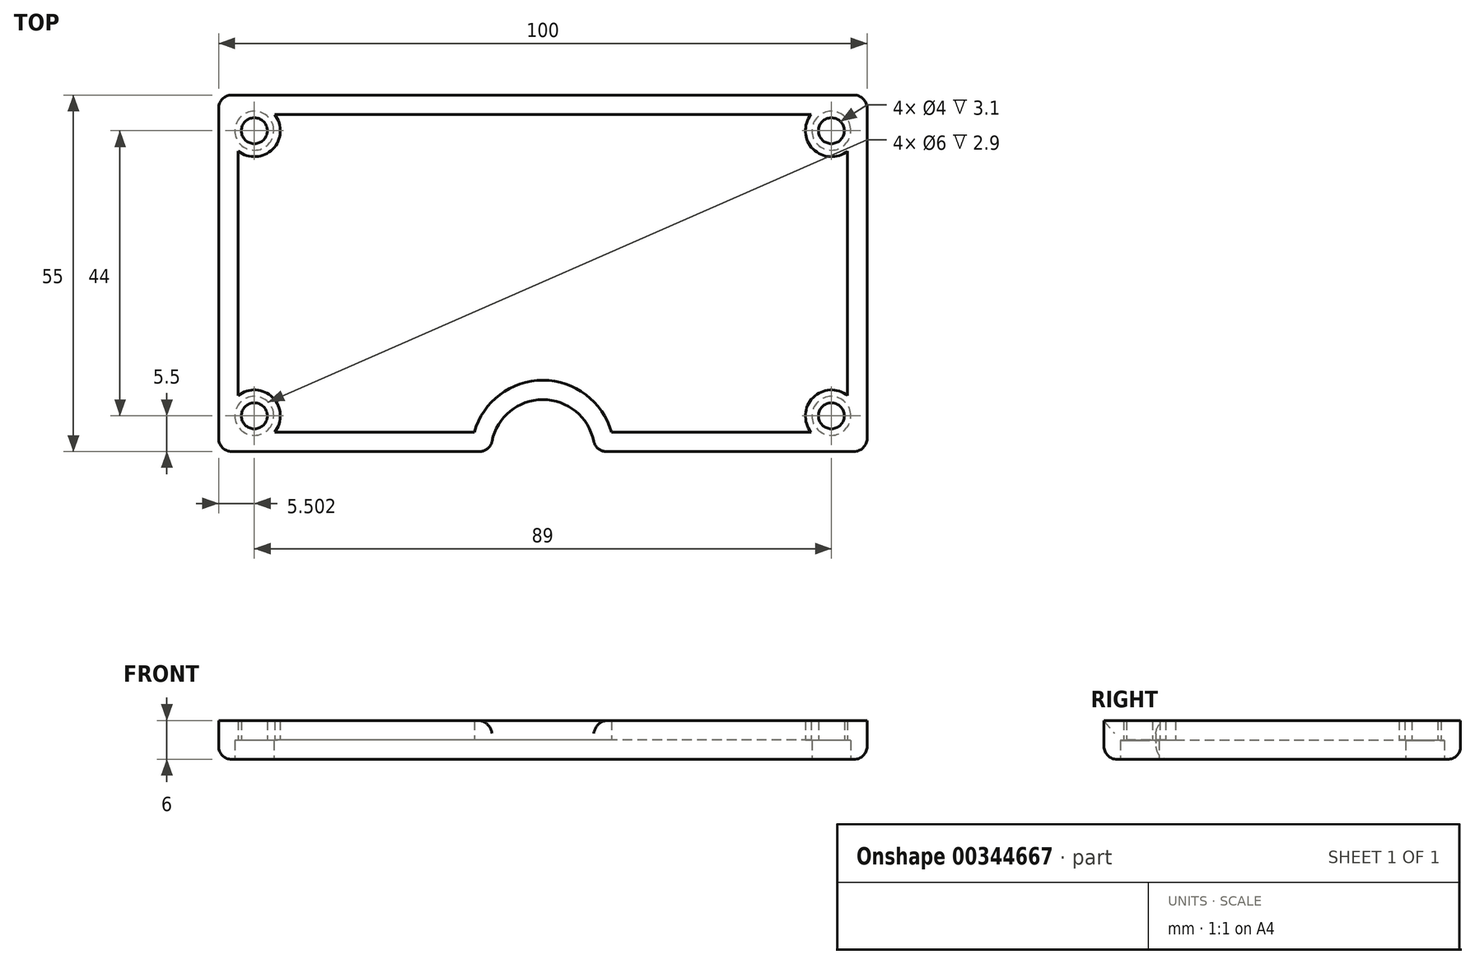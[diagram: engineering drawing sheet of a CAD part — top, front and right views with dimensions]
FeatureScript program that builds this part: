
annotation { "Feature Type Name" : "Feature", "Feature Type Description" : "" }
export const myFeature = defineFeature(function(context is Context, id is Id, definition is map)
    precondition{}
    {
        {
            var Q0;
            Q0=qCreatedBy(makeId("Top.planeOp"),FACE);
            var sketch = newSketch(context, id + "F0", { "sketchPlane" : qUnion([Q0])});
            skLineSegment(sketch, "E0.bottom", {"start": v(-50, 27.5) * mm, "end": v(50, 27.5) * mm});
            skLineSegment(sketch, "E0.top", {"start": v(-50, -27.5) * mm, "end": v(50, -27.5) * mm});
            skLineSegment(sketch, "E0.left", {"start": v(-50, 27.5) * mm, "end": v(-50, -27.5) * mm});
            skLineSegment(sketch, "E0.right", {"start": v(50, 27.5) * mm, "end": v(50, -27.5) * mm});
            skLineSegment(sketch, "E1.bottom", {"start": v(-35, 12.5) * mm, "end": v(-4, 12.5) * mm});
            skLineSegment(sketch, "E1.top", {"start": v(-35, -12.5) * mm, "end": v(-4, -12.5) * mm});
            skLineSegment(sketch, "E1.left", {"start": v(-35, 12.5) * mm, "end": v(-35, -12.5) * mm});
            skLineSegment(sketch, "E1.right", {"start": v(-4, 12.5) * mm, "end": v(-4, -12.5) * mm});
            skCircle(sketch, "E2", {"center": v(11, 12.5) * mm, "radius": 7 * mm});
            skCircle(sketch, "E3", {"center": v(11, -12.5) * mm, "radius": 7 * mm});
            skCircle(sketch, "E4", {"center": v(26.62, -12.5) * mm, "radius": 3 * mm});
            skCircle(sketch, "E5", {"center": v(26.62, 12.5) * mm, "radius": 3 * mm});
            skLineSegment(sketch, "E6.0", {"start": v(-41.38, 24.5) * mm, "end": v(41.38, 24.5) * mm});
            skLineSegment(sketch, "E6.1", {"start": v(-47, 18.88) * mm, "end": v(-47, -18.88) * mm});
            skLineSegment(sketch, "E6.2", {"start": v(-41.38, -24.5) * mm, "end": v(41.38, -24.5) * mm});
            skLineSegment(sketch, "E6.3", {"start": v(47, 18.88) * mm, "end": v(47, -18.88) * mm});
            skArc(sketch, "E7", {"start": v(41.38, 24.5) * mm, "mid": v(41.67, 19.17) * mm, "end": v(47, 18.88) * mm});
            skCircle(sketch, "E8", {"center": v(-44.5, 22) * mm, "radius": 2.5 * mm});
            skCircle(sketch, "E9", {"center": v(-44.5, -22) * mm, "radius": 2.5 * mm});
            skCircle(sketch, "E10", {"center": v(44.5, -22) * mm, "radius": 2.5 * mm});
            skArc(sketch, "E11", {"start": v(47, -18.88) * mm, "mid": v(41.67, -19.17) * mm, "end": v(41.38, -24.5) * mm});
            skCircle(sketch, "E12", {"center": v(44.5, 22) * mm, "radius": 2.5 * mm});
            skArc(sketch, "E13", {"start": v(-47, 18.88) * mm, "mid": v(-41.67, 19.17) * mm, "end": v(-41.38, 24.5) * mm});
            skArc(sketch, "E14", {"start": v(-41.38, -24.5) * mm, "mid": v(-41.67, -19.17) * mm, "end": v(-47, -18.88) * mm});
            skSolve(sketch);
        }
        {
            var Q0;
            Q0=makeQuery(id+"F0.imprint","IMPRINT",FACE,{"disambiguationData":[TD([[makeQuery(id+"F0.imprint","IMPRINT",EDGE,{"derivedFrom":sQuery(id+"F0.wireOp",EDGE,"E0.bottom")}),-1.0]])]});
            var Q1;
            Q1=makeQuery(id+"F0.imprint","IMPRINT",FACE,{"disambiguationData":[TD([[makeQuery(id+"F0.imprint","IMPRINT",EDGE,{"derivedFrom":sQuery(id+"F0.wireOp",EDGE,"E1.bottom")}),1.0]])]});
            var Q2;
            {var subQ3=sQuery(id+"F0.wireOp",EDGE,"E7");var subQ5=sQuery(id+"F0.wireOp",EDGE,"E6.0");var subQ8=makeQuery(id+"F0.imprint","INTERSECT",VERTEX,{"derivedFrom":[subQ5,subQ3]});Q2=makeQuery(id+"F0.imprint","IMPRINT",FACE,{"disambiguationData":[TD([[makeQuery(id+"F0.imprint","IMPRINT",EDGE,{"disambiguationData":[TD([[subQ8,-1.0]])],"derivedFrom":subQ5}),1.0]])]});}
            var Q3;
            {var subQ0=sQuery(id+"F0.wireOp",EDGE,"E6.3");var subQ1=sQuery(id+"F0.wireOp",EDGE,"E6.0");var subQ2=makeQuery(id+"F0.imprint","INTERSECT",VERTEX,{"derivedFrom":[subQ1,subQ0]});Q3=makeQuery(id+"F0.imprint","IMPRINT",FACE,{"disambiguationData":[TD([[makeQuery(id+"F0.imprint","IMPRINT",EDGE,{"disambiguationData":[TD([[subQ2,1.0]])],"derivedFrom":subQ1}),-1.0]])]});}
            var Q4;
            {var subQ0=sQuery(id+"F0.wireOp",EDGE,"E12");var subQ1=makeQuery(id+"F0.imprint","INTERSECT",VERTEX,{"derivedFrom":[sQuery(id+"F0.wireOp",EDGE,"E6.0"),subQ0]});Q4=makeQuery(id+"F0.imprint","IMPRINT",FACE,{"disambiguationData":[TD([[makeQuery(id+"F0.imprint","IMPRINT",EDGE,{"disambiguationData":[TD([[subQ1,1.0]])],"derivedFrom":subQ0}),1.0]])]});}
            var Q5;
            {var subQ0=sQuery(id+"F0.wireOp",EDGE,"E7");var subQ1=sQuery(id+"F0.wireOp",EDGE,"E6.0");var subQ2=makeQuery(id+"F0.imprint","INTERSECT",VERTEX,{"derivedFrom":[subQ1,subQ0]});Q5=makeQuery(id+"F0.imprint","IMPRINT",FACE,{"disambiguationData":[TD([[makeQuery(id+"F0.imprint","IMPRINT",EDGE,{"disambiguationData":[TD([[subQ2,-1.0]])],"derivedFrom":subQ1}),-1.0]])]});}
            var Q6;
            {var subQ1=sQuery(id+"F0.wireOp",EDGE,"E6.2");var subQ6=sQuery(id+"F0.wireOp",EDGE,"E11");var subQ8=makeQuery(id+"F0.imprint","INTERSECT",VERTEX,{"derivedFrom":[subQ1,subQ6]});Q6=makeQuery(id+"F0.imprint","IMPRINT",FACE,{"disambiguationData":[TD([[makeQuery(id+"F0.imprint","IMPRINT",EDGE,{"disambiguationData":[TD([[subQ8,-1.0]])],"derivedFrom":subQ1}),-1.0]])]});}
            var Q7;
            {var subQ0=sQuery(id+"F0.wireOp",EDGE,"E10");var subQ1=makeQuery(id+"F0.imprint","INTERSECT",VERTEX,{"derivedFrom":[sQuery(id+"F0.wireOp",EDGE,"E6.2"),subQ0]});Q7=makeQuery(id+"F0.imprint","IMPRINT",FACE,{"disambiguationData":[TD([[makeQuery(id+"F0.imprint","IMPRINT",EDGE,{"disambiguationData":[TD([[subQ1,1.0]])],"derivedFrom":subQ0}),1.0]])]});}
            var Q8;
            {var subQ0=sQuery(id+"F0.wireOp",EDGE,"E11");var subQ1=sQuery(id+"F0.wireOp",EDGE,"E6.2");var subQ2=makeQuery(id+"F0.imprint","INTERSECT",VERTEX,{"derivedFrom":[subQ1,subQ0]});Q8=makeQuery(id+"F0.imprint","IMPRINT",FACE,{"disambiguationData":[TD([[makeQuery(id+"F0.imprint","IMPRINT",EDGE,{"disambiguationData":[TD([[subQ2,-1.0]])],"derivedFrom":subQ1}),1.0]])]});}
            var Q9;
            {var subQ0=sQuery(id+"F0.wireOp",EDGE,"E6.3");var subQ1=sQuery(id+"F0.wireOp",EDGE,"E6.2");var subQ2=makeQuery(id+"F0.imprint","INTERSECT",VERTEX,{"derivedFrom":[subQ1,subQ0]});Q9=makeQuery(id+"F0.imprint","IMPRINT",FACE,{"disambiguationData":[TD([[makeQuery(id+"F0.imprint","IMPRINT",EDGE,{"disambiguationData":[TD([[subQ2,1.0]])],"derivedFrom":subQ1}),1.0]])]});}
            var Q10;
            {var subQ3=sQuery(id+"F0.wireOp",EDGE,"E14");var subQ5=sQuery(id+"F0.wireOp",EDGE,"E6.1");var subQ8=makeQuery(id+"F0.imprint","INTERSECT",VERTEX,{"derivedFrom":[subQ5,subQ3]});Q10=makeQuery(id+"F0.imprint","IMPRINT",FACE,{"disambiguationData":[TD([[makeQuery(id+"F0.imprint","IMPRINT",EDGE,{"disambiguationData":[TD([[subQ8,-1.0]])],"derivedFrom":subQ5}),-1.0]])]});}
            var Q11;
            {var subQ0=sQuery(id+"F0.wireOp",EDGE,"E6.2");var subQ1=sQuery(id+"F0.wireOp",EDGE,"E6.1");var subQ2=makeQuery(id+"F0.imprint","INTERSECT",VERTEX,{"derivedFrom":[subQ1,subQ0]});Q11=makeQuery(id+"F0.imprint","IMPRINT",FACE,{"disambiguationData":[TD([[makeQuery(id+"F0.imprint","IMPRINT",EDGE,{"disambiguationData":[TD([[subQ2,1.0]])],"derivedFrom":subQ1}),1.0]])]});}
            var Q12;
            {var subQ0=sQuery(id+"F0.wireOp",EDGE,"E14");var subQ1=sQuery(id+"F0.wireOp",EDGE,"E6.1");var subQ2=makeQuery(id+"F0.imprint","INTERSECT",VERTEX,{"derivedFrom":[subQ1,subQ0]});Q12=makeQuery(id+"F0.imprint","IMPRINT",FACE,{"disambiguationData":[TD([[makeQuery(id+"F0.imprint","IMPRINT",EDGE,{"disambiguationData":[TD([[subQ2,-1.0]])],"derivedFrom":subQ1}),1.0]])]});}
            var Q13;
            {var subQ0=sQuery(id+"F0.wireOp",EDGE,"E9");var subQ1=makeQuery(id+"F0.imprint","INTERSECT",VERTEX,{"derivedFrom":[sQuery(id+"F0.wireOp",EDGE,"E6.1"),subQ0]});Q13=makeQuery(id+"F0.imprint","IMPRINT",FACE,{"disambiguationData":[TD([[makeQuery(id+"F0.imprint","IMPRINT",EDGE,{"disambiguationData":[TD([[subQ1,-1.0]])],"derivedFrom":subQ0}),1.0]])]});}
            var Q14;
            {var subQ0=sQuery(id+"F0.wireOp",EDGE,"E8");var subQ1=makeQuery(id+"F0.imprint","INTERSECT",VERTEX,{"derivedFrom":[sQuery(id+"F0.wireOp",EDGE,"E6.0"),subQ0]});Q14=makeQuery(id+"F0.imprint","IMPRINT",FACE,{"disambiguationData":[TD([[makeQuery(id+"F0.imprint","IMPRINT",EDGE,{"disambiguationData":[TD([[subQ1,-1.0]])],"derivedFrom":subQ0}),1.0]])]});}
            var Q15;
            {var subQ0=sQuery(id+"F0.wireOp",EDGE,"E8");var subQ1=sQuery(id+"F0.wireOp",EDGE,"E6.0");var subQ2=makeQuery(id+"F0.imprint","INTERSECT",VERTEX,{"derivedFrom":[subQ1,subQ0]});Q15=makeQuery(id+"F0.imprint","IMPRINT",FACE,{"disambiguationData":[TD([[makeQuery(id+"F0.imprint","IMPRINT",EDGE,{"disambiguationData":[TD([[subQ2,-1.0]])],"derivedFrom":subQ1}),-1.0]])]});}
            var Q16;
            {var subQ1=sQuery(id+"F0.wireOp",EDGE,"E6.1");var subQ5=sQuery(id+"F0.wireOp",EDGE,"E6.0");var subQ8=makeQuery(id+"F0.imprint","INTERSECT",VERTEX,{"derivedFrom":[subQ5,subQ1]});Q16=makeQuery(id+"F0.imprint","IMPRINT",FACE,{"disambiguationData":[TD([[makeQuery(id+"F0.imprint","IMPRINT",EDGE,{"disambiguationData":[TD([[subQ8,-1.0]])],"derivedFrom":subQ5}),1.0]])]});}
            var Q17;
            {var subQ0=sQuery(id+"F0.wireOp",EDGE,"E6.1");var subQ1=sQuery(id+"F0.wireOp",EDGE,"E6.0");var subQ2=makeQuery(id+"F0.imprint","INTERSECT",VERTEX,{"derivedFrom":[subQ1,subQ0]});Q17=makeQuery(id+"F0.imprint","IMPRINT",FACE,{"disambiguationData":[TD([[makeQuery(id+"F0.imprint","IMPRINT",EDGE,{"disambiguationData":[TD([[subQ2,-1.0]])],"derivedFrom":subQ1}),-1.0]])]});}
            extrude(context, id + "F1", {"entities" : qUnion([Q0, Q1, Q2, Q3, Q4, Q5, Q6, Q7, Q8, Q9, Q10, Q11, Q12, Q13, Q14, Q15, Q16, Q17]), "depth" : 3 * mm});
        }
        {
            var Q0;
            Q0=makeQuery(id+"F0.imprint","IMPRINT",FACE,{"disambiguationData":[TD([[makeQuery(id+"F0.imprint","IMPRINT",EDGE,{"derivedFrom":sQuery(id+"F0.wireOp",EDGE,"E0.bottom")}),-1.0]])]});
            extrude(context, id + "F2", {"entities" : qUnion([Q0]), "operationType" : NewBodyOperationType.ADD, "oppositeDirection" : true, "depth" : 110 * mm});
        }
        {
            var Q0;
            Q0=makeQuery(id+"F0.imprint","IMPRINT",FACE,{"disambiguationData":[TD([[makeQuery(id+"F0.imprint","IMPRINT",EDGE,{"derivedFrom":sQuery(id+"F0.wireOp",EDGE,"E1.bottom")}),1.0]])]});
            var sketch = newSketch(context, id + "F3", { "sketchPlane" : qUnion([Q0])});
            skCircle(sketch, "E15", {"center": v(37, 0.5) * mm, "radius": 3.5 * mm});
            skCircle(sketch, "E16", {"center": v(7, 0.5) * mm, "radius": 3.5 * mm});
            skCircle(sketch, "E17", {"center": v(37, 0.5) * mm, "radius": 1.5 * mm});
            skCircle(sketch, "E18", {"center": v(7, 0.5) * mm, "radius": 1.5 * mm});
            skLineSegment(sketch, "E19.bottom", {"start": v(14.15, 20.5) * mm, "end": v(-35.5, 20.5) * mm});
            skLineSegment(sketch, "E19.top", {"start": v(14.15, 24.5) * mm, "end": v(-35.5, 24.5) * mm});
            skLineSegment(sketch, "E19.left", {"start": v(14.15, 20.5) * mm, "end": v(14.15, 24.5) * mm});
            skLineSegment(sketch, "E19.right", {"start": v(-35.5, 20.5) * mm, "end": v(-35.5, 24.5) * mm});
            skLineSegment(sketch, "E20.bottom", {"start": v(13.98, -14.5) * mm, "end": v(-35.42, -14.5) * mm});
            skLineSegment(sketch, "E20.top", {"start": v(13.98, -24.5) * mm, "end": v(-35.42, -24.5) * mm});
            skLineSegment(sketch, "E20.left", {"start": v(13.98, -14.5) * mm, "end": v(13.98, -24.5) * mm});
            skLineSegment(sketch, "E20.right", {"start": v(-35.42, -14.5) * mm, "end": v(-35.42, -24.5) * mm});
            skCircle(sketch, "E21", {"center": v(-2.5, 22.5) * mm, "radius": 1 * mm});
            skCircle(sketch, "E22", {"center": v(-2.5, -16.5) * mm, "radius": 1 * mm});
            skCircle(sketch, "E23", {"center": v(-41.5, -16.5) * mm, "radius": 1 * mm});
            skCircle(sketch, "E24", {"center": v(-41.5, 22.5) * mm, "radius": 1 * mm});
            skSolve(sketch);
        }
        {
            var Q0;
            {var subQ0=sQuery(id+"F3.wireOp",EDGE,"E19.left");Q0=makeQuery(id+"F3.imprint","IMPRINT",FACE,{"disambiguationData":[TD([[makeQuery(id+"F3.imprint","IMPRINT",EDGE,{"derivedFrom":subQ0}),1.0]])]});}
            var Q1;
            Q1=makeQuery(id+"F3.imprint","IMPRINT",FACE,{"disambiguationData":[TD([[makeQuery(id+"F3.imprint","IMPRINT",EDGE,{"derivedFrom":sQuery(id+"F3.wireOp",EDGE,"E16")}),1.0]])]});
            var Q2;
            Q2=makeQuery(id+"F3.imprint","IMPRINT",FACE,{"disambiguationData":[TD([[makeQuery(id+"F3.imprint","IMPRINT",EDGE,{"derivedFrom":sQuery(id+"F3.wireOp",EDGE,"E15")}),1.0]])]});
            var Q3;
            {var subQ0=sQuery(id+"F3.wireOp",EDGE,"E20.left");Q3=makeQuery(id+"F3.imprint","IMPRINT",FACE,{"disambiguationData":[TD([[makeQuery(id+"F3.imprint","IMPRINT",EDGE,{"derivedFrom":subQ0}),-1.0]])]});}
            extrude(context, id + "F4", {"entities" : qUnion([Q0, Q1, Q2, Q3]), "operationType" : NewBodyOperationType.ADD, "oppositeDirection" : true, "depth" : 4 * mm});
        }
        {
            var Q0;
            {var subQ0=sQuery(id+"F0.wireOp",EDGE,"E0.right");var subQ1=sQuery(id+"F0.wireOp",EDGE,"E0.bottom");Q0=makeQuery(id+"F2.boolean.opBoolean","MERGE",EDGE,{"derivedFrom":[makeQuery(id+"F1.opExtrude","SWEPT_EDGE",EDGE,{"disambiguationData":[OSD([subQ1,subQ0])]}),makeQuery(id+"F2.opExtrude","SWEPT_EDGE",EDGE,{"disambiguationData":[OSD([subQ1,subQ0])]})]});}
            var Q1;
            {var subQ0=sQuery(id+"F0.wireOp",EDGE,"E0.left");var subQ1=sQuery(id+"F0.wireOp",EDGE,"E0.bottom");Q1=makeQuery(id+"F2.boolean.opBoolean","MERGE",EDGE,{"derivedFrom":[makeQuery(id+"F1.opExtrude","SWEPT_EDGE",EDGE,{"disambiguationData":[OSD([subQ1,subQ0])]}),makeQuery(id+"F2.opExtrude","SWEPT_EDGE",EDGE,{"disambiguationData":[OSD([subQ1,subQ0])]})]});}
            var Q2;
            {var subQ0=sQuery(id+"F0.wireOp",EDGE,"E0.left");var subQ1=sQuery(id+"F0.wireOp",EDGE,"E0.top");Q2=makeQuery(id+"F2.boolean.opBoolean","MERGE",EDGE,{"derivedFrom":[makeQuery(id+"F1.opExtrude","SWEPT_EDGE",EDGE,{"disambiguationData":[OSD([subQ1,subQ0])]}),makeQuery(id+"F2.opExtrude","SWEPT_EDGE",EDGE,{"disambiguationData":[OSD([subQ1,subQ0])]})]});}
            var Q3;
            {var subQ0=sQuery(id+"F0.wireOp",EDGE,"E0.right");var subQ1=sQuery(id+"F0.wireOp",EDGE,"E0.top");Q3=makeQuery(id+"F2.boolean.opBoolean","MERGE",EDGE,{"derivedFrom":[makeQuery(id+"F1.opExtrude","SWEPT_EDGE",EDGE,{"disambiguationData":[OSD([subQ1,subQ0])]}),makeQuery(id+"F2.opExtrude","SWEPT_EDGE",EDGE,{"disambiguationData":[OSD([subQ1,subQ0])]})]});}
            var Q4;
            Q4=makeQuery(id+"F1.opExtrude","CAP_EDGE",EDGE,{"disambiguationData":[OSD([sQuery(id+"F0.wireOp",EDGE,"E0.bottom")])],"isStart":false});
            var Q5;
            Q5=makeQuery(id+"F1.opExtrude","CAP_EDGE",EDGE,{"disambiguationData":[OSD([sQuery(id+"F0.wireOp",EDGE,"E0.left")])],"isStart":false});
            var Q6;
            Q6=makeQuery(id+"F1.opExtrude","CAP_EDGE",EDGE,{"disambiguationData":[OSD([sQuery(id+"F0.wireOp",EDGE,"E0.top")])],"isStart":false});
            var Q7;
            Q7=makeQuery(id+"F1.opExtrude","CAP_EDGE",EDGE,{"disambiguationData":[OSD([sQuery(id+"F0.wireOp",EDGE,"E0.right")])],"isStart":false});
            fillet(context, id + "F5", {"entities" : qUnion([Q0, Q1, Q2, Q3, Q4, Q5, Q6, Q7]), "radius" : 2 * mm, "tangentPropagation" : true, "allowEdgeOverflow" : false});
        }
        {
            var Q0;
            Q0=qCreatedBy(makeId("Top.planeOp"),FACE);
            cPlane(context, id + "F6", {"entities" : qUnion([Q0]), "cplaneType" : CPlaneType.OFFSET, "offset" : 150 * mm, "oppositeDirection" : true, "width" : 150 * mm, "height" : 150 * mm});
        }
        {
            var Q0;
            Q0=qCreatedBy(id+"F6.planeOp",FACE);
            var sketch = newSketch(context, id + "F7", { "sketchPlane" : qUnion([Q0])});
            skLineSegment(sketch, "E25.bottom", {"start": v(-50.47, 27.5) * mm, "end": v(49.53, 27.5) * mm});
            skLineSegment(sketch, "E25.top", {"start": v(-50.47, -27.5) * mm, "end": v(-8.47, -27.5) * mm});
            skLineSegment(sketch, "E25.left", {"start": v(-50.47, 27.5) * mm, "end": v(-50.47, -27.5) * mm});
            skLineSegment(sketch, "E25.right", {"start": v(49.53, 27.5) * mm, "end": v(49.53, -27.5) * mm});
            skLineSegment(sketch, "E26.0", {"start": v(-41.85, 24.5) * mm, "end": v(40.9, 24.5) * mm});
            skLineSegment(sketch, "E26.1", {"start": v(-47.47, 18.88) * mm, "end": v(-47.47, -18.88) * mm});
            skLineSegment(sketch, "E26.2", {"start": v(-41.85, -24.5) * mm, "end": v(-11.05, -24.5) * mm});
            skLineSegment(sketch, "E26.3", {"start": v(46.53, 18.88) * mm, "end": v(46.53, -18.88) * mm});
            skArc(sketch, "E27", {"start": v(40.9, 24.5) * mm, "mid": v(41.2, 19.17) * mm, "end": v(46.53, 18.88) * mm});
            skCircle(sketch, "E28", {"center": v(-44.97, 22) * mm, "radius": 2 * mm});
            skCircle(sketch, "E29", {"center": v(-44.97, -22) * mm, "radius": 2 * mm});
            skCircle(sketch, "E30", {"center": v(44.03, -22) * mm, "radius": 2 * mm});
            skArc(sketch, "E31", {"start": v(46.53, -18.88) * mm, "mid": v(41.2, -19.17) * mm, "end": v(40.9, -24.5) * mm});
            skCircle(sketch, "E32", {"center": v(44.03, 22) * mm, "radius": 2 * mm});
            skArc(sketch, "E33", {"start": v(-41.85, -24.5) * mm, "mid": v(-42.14, -19.17) * mm, "end": v(-47.47, -18.88) * mm});
            skCircle(sketch, "E34", {"center": v(-44.97, -22) * mm, "radius": 3 * mm});
            skCircle(sketch, "E35", {"center": v(44.03, -22) * mm, "radius": 3 * mm});
            skCircle(sketch, "E36", {"center": v(44.03, 22) * mm, "radius": 3 * mm});
            skArc(sketch, "E37", {"start": v(-47.47, 18.88) * mm, "mid": v(-42.14, 19.17) * mm, "end": v(-41.85, 24.5) * mm});
            skCircle(sketch, "E38", {"center": v(-44.97, 22) * mm, "radius": 3 * mm});
            skArc(sketch, "E39", {"start": v(10.12, -24.5) * mm, "mid": v(-0.47, -16.5) * mm, "end": v(-11.05, -24.5) * mm});
            skArc(sketch, "E40", {"start": v(7.53, -27.5) * mm, "mid": v(-0.47, -19.5) * mm, "end": v(-8.47, -27.5) * mm});
            skLineSegment(sketch, "E41.trimOffspring", {"start": v(7.53, -27.5) * mm, "end": v(49.53, -27.5) * mm});
            skLineSegment(sketch, "E42.trimOffspring", {"start": v(10.12, -24.5) * mm, "end": v(40.9, -24.5) * mm});
            skSolve(sketch);
        }
        {
            var Q0;
            Q0=makeQuery(id+"F7.imprint","IMPRINT",FACE,{"disambiguationData":[TD([[makeQuery(id+"F7.imprint","IMPRINT",EDGE,{"derivedFrom":sQuery(id+"F7.wireOp",EDGE,"E26.0")}),-1.0]])]});
            var Q1;
            Q1=makeQuery(id+"F7.imprint","IMPRINT",FACE,{"disambiguationData":[TD([[makeQuery(id+"F7.imprint","IMPRINT",EDGE,{"derivedFrom":sQuery(id+"F7.wireOp",EDGE,"E25.bottom")}),-1.0]])]});
            extrude(context, id + "F8", {"entities" : qUnion([Q0, Q1]), "depth" : 3 * mm});
        }
        {
            var Q0;
            Q0=makeQuery(id+"F7.imprint","IMPRINT",FACE,{"disambiguationData":[TD([[makeQuery(id+"F7.imprint","IMPRINT",EDGE,{"derivedFrom":sQuery(id+"F7.wireOp",EDGE,"E25.bottom")}),-1.0]])]});
            var Q1;
            Q1=makeQuery(id+"F7.imprint","IMPRINT",FACE,{"disambiguationData":[TD([[makeQuery(id+"F7.imprint","IMPRINT",EDGE,{"derivedFrom":sQuery(id+"F7.wireOp",EDGE,"E29")}),-1.0]])]});
            var Q2;
            Q2=makeQuery(id+"F7.imprint","IMPRINT",FACE,{"disambiguationData":[TD([[makeQuery(id+"F7.imprint","IMPRINT",EDGE,{"derivedFrom":sQuery(id+"F7.wireOp",EDGE,"E28")}),-1.0]])]});
            var Q3;
            Q3=makeQuery(id+"F7.imprint","IMPRINT",FACE,{"disambiguationData":[TD([[makeQuery(id+"F7.imprint","IMPRINT",EDGE,{"derivedFrom":sQuery(id+"F7.wireOp",EDGE,"E32")}),-1.0]])]});
            var Q4;
            Q4=makeQuery(id+"F7.imprint","IMPRINT",FACE,{"disambiguationData":[TD([[makeQuery(id+"F7.imprint","IMPRINT",EDGE,{"derivedFrom":sQuery(id+"F7.wireOp",EDGE,"E30")}),-1.0]])]});
            extrude(context, id + "F9", {"entities" : qUnion([Q0, Q1, Q2, Q3, Q4]), "operationType" : NewBodyOperationType.ADD, "depth" : 6 * mm});
        }
        {
            var Q0;
            {var subQ0=sQuery(id+"F0.wireOp",EDGE,"E3");Q0=makeQuery(id+"F4.boolean.opBoolean","MERGE",BODY,{"derivedFrom":[makeQuery(id+"F1.opExtrude","SWEPT_BODY",BODY,{"disambiguationData":[OSD([sQuery(id+"F0.wireOp",EDGE,"E0.bottom"),sQuery(id+"F0.wireOp",EDGE,"E0.top"),sQuery(id+"F0.wireOp",EDGE,"E0.left"),sQuery(id+"F0.wireOp",EDGE,"E0.right"),sQuery(id+"F0.wireOp",EDGE,"E1.bottom"),sQuery(id+"F0.wireOp",EDGE,"E1.top"),sQuery(id+"F0.wireOp",EDGE,"E1.left"),sQuery(id+"F0.wireOp",EDGE,"E1.right"),sQuery(id+"F0.wireOp",EDGE,"E2"),subQ0,sQuery(id+"F0.wireOp",EDGE,"E4"),sQuery(id+"F0.wireOp",EDGE,"E5")])]}),makeQuery(id+"F4.opExtrude","SWEPT_BODY",BODY,{"disambiguationData":[OSD([sQuery(id+"F3.wireOp",EDGE,"E15"),sQuery(id+"F3.wireOp",EDGE,"E17")])]}),makeQuery(id+"F4.opExtrude","SWEPT_BODY",BODY,{"disambiguationData":[OSD([sQuery(id+"F3.wireOp",EDGE,"E16"),sQuery(id+"F3.wireOp",EDGE,"E18")])]}),makeQuery(id+"F4.opExtrude","SWEPT_BODY",BODY,{"disambiguationData":[OSD([sQuery(id+"F3.wireOp",EDGE,"E19.bottom"),sQuery(id+"F3.wireOp",EDGE,"E19.top"),sQuery(id+"F3.wireOp",EDGE,"E19.left"),sQuery(id+"F3.wireOp",EDGE,"E19.right"),sQuery(id+"F3.wireOp",EDGE,"E21")])]}),makeQuery(id+"F4.opExtrude","SWEPT_BODY",BODY,{"disambiguationData":[OSD([subQ0,sQuery(id+"F3.wireOp",EDGE,"E20.bottom"),sQuery(id+"F3.wireOp",EDGE,"E20.left")])]})]});}
            deleteBodies(context, id + "F10", {"entities" : qUnion([Q0])});
        }
        {
            var Q0;
            Q0=makeQuery(id+"F7.imprint","IMPRINT",FACE,{"disambiguationData":[TD([[makeQuery(id+"F7.imprint","IMPRINT",EDGE,{"derivedFrom":sQuery(id+"F7.wireOp",EDGE,"E28")}),-1.0]])]});
            var Q1;
            Q1=makeQuery(id+"F7.imprint","IMPRINT",FACE,{"disambiguationData":[TD([[makeQuery(id+"F7.imprint","IMPRINT",EDGE,{"derivedFrom":sQuery(id+"F7.wireOp",EDGE,"E32")}),-1.0]])]});
            var Q2;
            Q2=makeQuery(id+"F7.imprint","IMPRINT",FACE,{"disambiguationData":[TD([[makeQuery(id+"F7.imprint","IMPRINT",EDGE,{"derivedFrom":sQuery(id+"F7.wireOp",EDGE,"E30")}),-1.0]])]});
            var Q3;
            Q3=makeQuery(id+"F7.imprint","IMPRINT",FACE,{"disambiguationData":[TD([[makeQuery(id+"F7.imprint","IMPRINT",EDGE,{"derivedFrom":sQuery(id+"F7.wireOp",EDGE,"E29")}),-1.0]])]});
            extrude(context, id + "F11", {"entities" : qUnion([Q0, Q1, Q2, Q3]), "operationType" : NewBodyOperationType.REMOVE, "depth" : 2.9 * mm});
        }
        {
            var Q0;
            {var subQ0=sQuery(id+"F7.wireOp",EDGE,"E25.right");var subQ1=sQuery(id+"F7.wireOp",EDGE,"E25.top");Q0=makeQuery(id+"F9.boolean.opBoolean","MERGE",EDGE,{"derivedFrom":[makeQuery(id+"F8.opExtrude","SWEPT_EDGE",EDGE,{"disambiguationData":[OSD([subQ1,subQ0])]}),makeQuery(id+"F9.opExtrude","SWEPT_EDGE",EDGE,{"disambiguationData":[OSD([subQ1,subQ0])]})]});}
            var Q1;
            {var subQ0=sQuery(id+"F7.wireOp",EDGE,"E25.left");var subQ1=sQuery(id+"F7.wireOp",EDGE,"E25.top");Q1=makeQuery(id+"F9.boolean.opBoolean","MERGE",EDGE,{"derivedFrom":[makeQuery(id+"F8.opExtrude","SWEPT_EDGE",EDGE,{"disambiguationData":[OSD([subQ1,subQ0])]}),makeQuery(id+"F9.opExtrude","SWEPT_EDGE",EDGE,{"disambiguationData":[OSD([subQ1,subQ0])]})]});}
            var Q2;
            {var subQ0=sQuery(id+"F7.wireOp",EDGE,"E25.left");var subQ1=sQuery(id+"F7.wireOp",EDGE,"E25.bottom");Q2=makeQuery(id+"F9.boolean.opBoolean","MERGE",EDGE,{"derivedFrom":[makeQuery(id+"F8.opExtrude","SWEPT_EDGE",EDGE,{"disambiguationData":[OSD([subQ1,subQ0])]}),makeQuery(id+"F9.opExtrude","SWEPT_EDGE",EDGE,{"disambiguationData":[OSD([subQ1,subQ0])]})]});}
            var Q3;
            {var subQ0=sQuery(id+"F7.wireOp",EDGE,"E25.right");var subQ1=sQuery(id+"F7.wireOp",EDGE,"E25.bottom");Q3=makeQuery(id+"F9.boolean.opBoolean","MERGE",EDGE,{"derivedFrom":[makeQuery(id+"F8.opExtrude","SWEPT_EDGE",EDGE,{"disambiguationData":[OSD([subQ1,subQ0])]}),makeQuery(id+"F9.opExtrude","SWEPT_EDGE",EDGE,{"disambiguationData":[OSD([subQ1,subQ0])]})]});}
            var Q4;
            Q4=makeQuery(id+"F8.opExtrude","CAP_EDGE",EDGE,{"disambiguationData":[OSD([sQuery(id+"F7.wireOp",EDGE,"E25.right")])],"isStart":true});
            var Q5;
            Q5=makeQuery(id+"F8.opExtrude","CAP_EDGE",EDGE,{"disambiguationData":[OSD([sQuery(id+"F7.wireOp",EDGE,"E25.top")])],"isStart":true});
            var Q6;
            Q6=makeQuery(id+"F8.opExtrude","CAP_EDGE",EDGE,{"disambiguationData":[OSD([sQuery(id+"F7.wireOp",EDGE,"E25.left")])],"isStart":true});
            var Q7;
            Q7=makeQuery(id+"F8.opExtrude","CAP_EDGE",EDGE,{"disambiguationData":[OSD([sQuery(id+"F7.wireOp",EDGE,"E25.bottom")])],"isStart":true});
            var Q8;
            {var subQ0=sQuery(id+"F7.wireOp",EDGE,"E41.trimOffspring");var subQ1=sQuery(id+"F7.wireOp",EDGE,"E40");Q8=makeQuery(id+"F9.boolean.opBoolean","MERGE",EDGE,{"derivedFrom":[makeQuery(id+"F8.opExtrude","SWEPT_EDGE",EDGE,{"disambiguationData":[OSD([subQ1,subQ0])]}),makeQuery(id+"F9.opExtrude","SWEPT_EDGE",EDGE,{"disambiguationData":[OSD([subQ1,subQ0])]})]});}
            var Q9;
            Q9=makeQuery(id+"F8.opExtrude","CAP_EDGE",EDGE,{"disambiguationData":[OSD([sQuery(id+"F7.wireOp",EDGE,"E41.trimOffspring")])],"isStart":true});
            var Q10;
            Q10=makeQuery(id+"F8.opExtrude","CAP_EDGE",EDGE,{"disambiguationData":[OSD([sQuery(id+"F7.wireOp",EDGE,"E40")])],"isStart":true});
            var Q11;
            Q11=makeQuery(id+"F9.opExtrude","CAP_EDGE",EDGE,{"disambiguationData":[OSD([sQuery(id+"F7.wireOp",EDGE,"E40")])],"isStart":false});
            fillet(context, id + "F12", {"entities" : qUnion([Q0, Q1, Q2, Q3, Q4, Q5, Q6, Q7, Q8, Q9, Q10, Q11]), "radius" : 2 * mm, "tangentPropagation" : true, "allowEdgeOverflow" : false});
        }
    });
